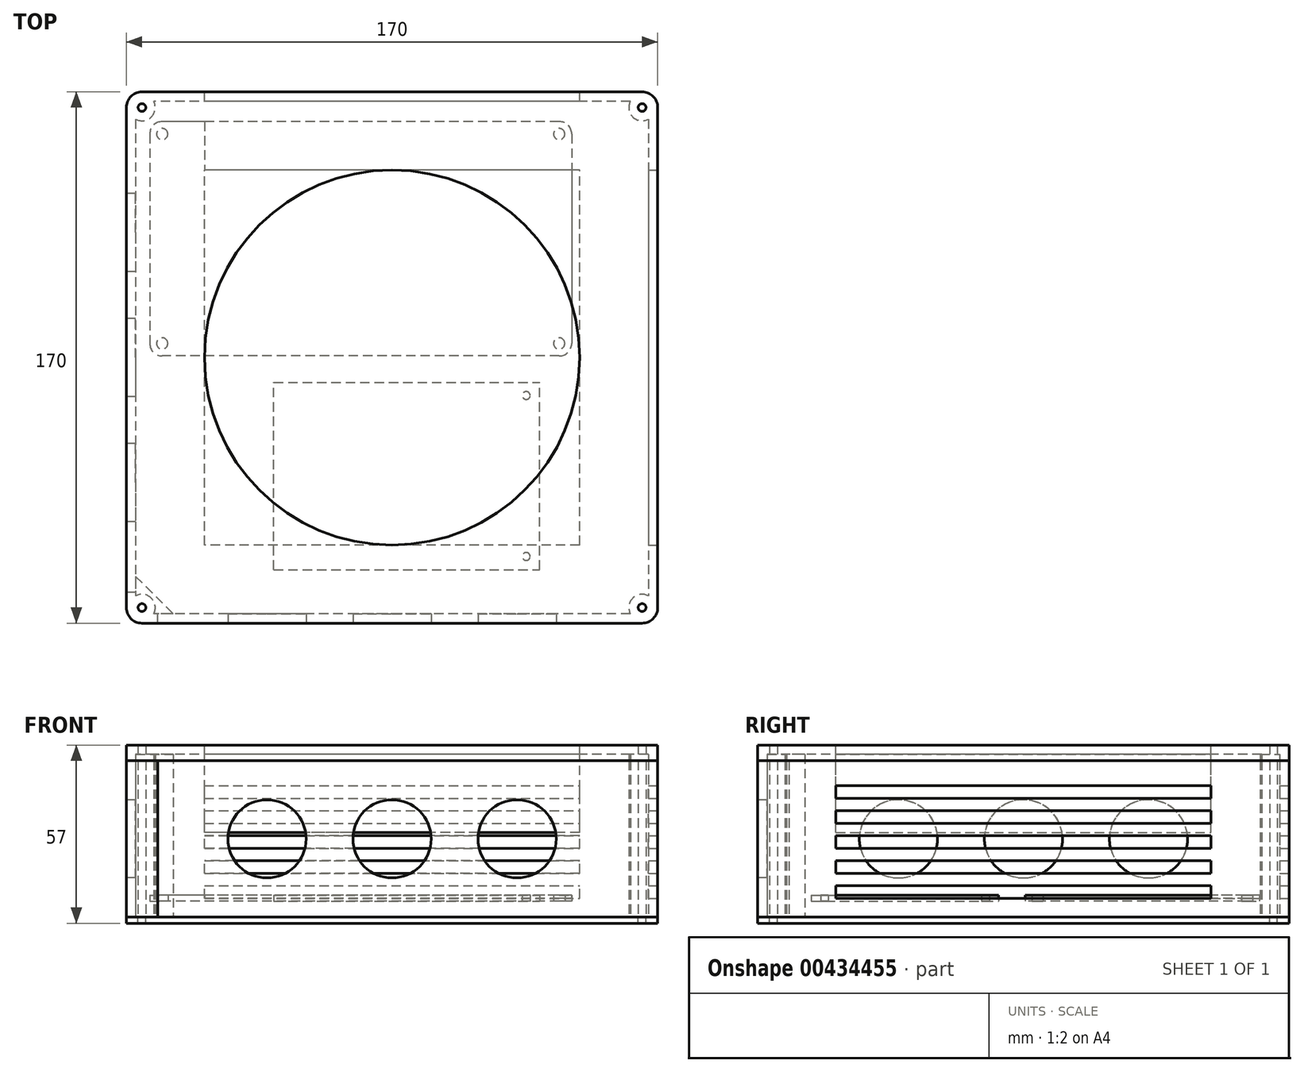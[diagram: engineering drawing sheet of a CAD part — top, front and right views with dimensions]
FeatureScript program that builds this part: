
annotation { "Feature Type Name" : "Feature", "Feature Type Description" : "" }
export const myFeature = defineFeature(function(context is Context, id is Id, definition is map)
    precondition{}
    {
        {
            var Q0;
            Q0=qCreatedBy(makeId("Top.planeOp"),FACE);
            var sketch = newSketch(context, id + "F0", { "sketchPlane" : qUnion([Q0])});
            skLineSegment(sketch, "E0.bottom", {"start": v(63.5, 37.5) * mm, "end": v(-63.5, 37.5) * mm});
            skLineSegment(sketch, "E0.top", {"start": v(63.5, -37.5) * mm, "end": v(-63.5, -37.5) * mm});
            skLineSegment(sketch, "E0.left", {"start": v(67.5, 33.5) * mm, "end": v(67.5, -33.5) * mm});
            skLineSegment(sketch, "E0.right", {"start": v(-67.5, 33.5) * mm, "end": v(-67.5, -33.5) * mm});
            skPoint(sketch, "E0.middle", {"position": v(0, 0) * mm});
            skCircle(sketch, "E1", {"center": v(63.5, 33.5) * mm, "radius": 1.8 * mm});
            skCircle(sketch, "E2.MirrorC", {"center": v(-63.5, 33.5) * mm, "radius": 1.8 * mm});
            skCircle(sketch, "E3.MirrorC", {"center": v(63.5, -33.5) * mm, "radius": 1.8 * mm});
            skCircle(sketch, "E4.MirrorC", {"center": v(-63.5, -33.5) * mm, "radius": 1.8 * mm});
            skPoint(sketch, "E5.visualSharp", {"position": v(-67.5, 37.5) * mm});
            skArc(sketch, "E5.filletArc", {"start": v(-63.5, 37.5) * mm, "mid": v(-66.33, 36.33) * mm, "end": v(-67.5, 33.5) * mm});
            skPoint(sketch, "E6.visualSharp", {"position": v(-67.5, -37.5) * mm});
            skArc(sketch, "E6.filletArc", {"start": v(-67.5, -33.5) * mm, "mid": v(-66.33, -36.33) * mm, "end": v(-63.5, -37.5) * mm});
            skPoint(sketch, "E7.visualSharp", {"position": v(67.5, -37.5) * mm});
            skArc(sketch, "E7.filletArc", {"start": v(63.5, -37.5) * mm, "mid": v(66.33, -36.33) * mm, "end": v(67.5, -33.5) * mm});
            skPoint(sketch, "E8.visualSharp", {"position": v(67.5, 37.5) * mm});
            skArc(sketch, "E8.filletArc", {"start": v(67.5, 33.5) * mm, "mid": v(66.33, 36.33) * mm, "end": v(63.5, 37.5) * mm});
            skSolve(sketch);
        }
        {
            var Q0;
            Q0 = qSketchRegion(id + "F0", true);
            extrude(context, id + "F1", {"entities" : qUnion([Q0]), "depth" : 2 * mm});
        }
        {
            var Q0;
            Q0=qCreatedBy(makeId("Top.planeOp"),FACE);
            var sketch = newSketch(context, id + "F2", { "sketchPlane" : qUnion([Q0])});
            skLineSegment(sketch, "E9.bottom", {"start": v(-42.5, -30) * mm, "end": v(42.5, -30) * mm});
            skLineSegment(sketch, "E9.top", {"start": v(-42.5, 30) * mm, "end": v(42.5, 30) * mm});
            skLineSegment(sketch, "E9.left", {"start": v(-42.5, -30) * mm, "end": v(-42.5, 30) * mm});
            skLineSegment(sketch, "E9.right", {"start": v(42.5, -30) * mm, "end": v(42.5, 30) * mm});
            skPoint(sketch, "E9.middle", {"position": v(0, 0) * mm});
            skCircle(sketch, "E10", {"center": v(38.25, -25.75) * mm, "radius": 1.25 * mm});
            skCircle(sketch, "E11.MirrorC", {"center": v(38.25, 25.75) * mm, "radius": 1.25 * mm});
            skSolve(sketch);
        }
        {
            var Q0;
            Q0=makeQuery(id+"F2.imprint","IMPRINT",FACE,{"disambiguationData":[TD([[makeQuery(id+"F2.imprint","IMPRINT",EDGE,{"derivedFrom":sQuery(id+"F2.wireOp",EDGE,"E9.bottom")}),1.0]])]});
            extrude(context, id + "F3", {"entities" : qUnion([Q0]), "depth" : 2 * mm});
        }
        {
            var Q0;
            Q0=makeQuery(id+"F1.opExtrude","SWEPT_BODY",BODY,{"disambiguationData":[OSD([sQuery(id+"F0.wireOp",EDGE,"E0.bottom"),sQuery(id+"F0.wireOp",EDGE,"E0.top"),sQuery(id+"F0.wireOp",EDGE,"E0.left"),sQuery(id+"F0.wireOp",EDGE,"E0.right"),sQuery(id+"F0.wireOp",EDGE,"E1"),sQuery(id+"F0.wireOp",EDGE,"E2.MirrorC"),sQuery(id+"F0.wireOp",EDGE,"E3.MirrorC"),sQuery(id+"F0.wireOp",EDGE,"E4.MirrorC"),sQuery(id+"F0.wireOp",EDGE,"E5.filletArc"),sQuery(id+"F0.wireOp",EDGE,"E6.filletArc"),sQuery(id+"F0.wireOp",EDGE,"E7.filletArc"),sQuery(id+"F0.wireOp",EDGE,"E8.filletArc")])]});
            transform(context, id + "F4", {"entities" : qUnion([Q0]), "transformType" : TransformType.TRANSLATION_3D, "dx" : -10 * mm, "dy" : 38 * mm, "dz" : 5 * mm, "makeCopy" : false});
        }
        {
            var Q0;
            Q0=makeQuery(id+"F3.opExtrude","SWEPT_BODY",BODY,{"disambiguationData":[OSD([sQuery(id+"F2.wireOp",EDGE,"E9.bottom"),sQuery(id+"F2.wireOp",EDGE,"E9.top"),sQuery(id+"F2.wireOp",EDGE,"E9.left"),sQuery(id+"F2.wireOp",EDGE,"E9.right"),sQuery(id+"F2.wireOp",EDGE,"E10"),sQuery(id+"F2.wireOp",EDGE,"E11.MirrorC")])]});
            transform(context, id + "F5", {"entities" : qUnion([Q0]), "transformType" : TransformType.TRANSLATION_3D, "dx" : 4.7 * mm, "dy" : -37.9 * mm, "dz" : 5 * mm, "makeCopy" : false});
        }
        {
            var Q0;
            Q0=qCreatedBy(makeId("Top.planeOp"),FACE);
            var sketch = newSketch(context, id + "F6", { "sketchPlane" : qUnion([Q0])});
            skLineSegment(sketch, "E12.bottom", {"start": v(85, 85) * mm, "end": v(-85, 85) * mm});
            skLineSegment(sketch, "E12.top", {"start": v(85, -85) * mm, "end": v(-85, -85) * mm});
            skLineSegment(sketch, "E12.left", {"start": v(85, 85) * mm, "end": v(85, -85) * mm});
            skLineSegment(sketch, "E12.right", {"start": v(-85, 85) * mm, "end": v(-85, -85) * mm});
            skPoint(sketch, "E12.middle", {"position": v(0, 0) * mm});
            skCircle(sketch, "E13", {"center": v(-80, -80) * mm, "radius": 1.25 * mm});
            skCircle(sketch, "E14.MirrorC", {"center": v(-80, 80) * mm, "radius": 1.25 * mm});
            skCircle(sketch, "E15.MirrorC", {"center": v(80, -80) * mm, "radius": 1.25 * mm});
            skCircle(sketch, "E16.MirrorC", {"center": v(80, 80) * mm, "radius": 1.25 * mm});
            skSolve(sketch);
        }
        {
            var Q0;
            Q0 = qSketchRegion(id + "F6", true);
            extrude(context, id + "F7", {"entities" : qUnion([Q0]), "depth" : 50 * mm, "offsetDistance" : 25 * mm});
        }
        {
            var Q0;
            Q0=makeQuery(id+"F7.opExtrude","CAP_FACE",FACE,{"disambiguationData":[OSD([sQuery(id+"F6.wireOp",EDGE,"E12.bottom"),sQuery(id+"F6.wireOp",EDGE,"E12.top"),sQuery(id+"F6.wireOp",EDGE,"E12.left"),sQuery(id+"F6.wireOp",EDGE,"E12.right"),sQuery(id+"F6.wireOp",EDGE,"E13"),sQuery(id+"F6.wireOp",EDGE,"E14.MirrorC"),sQuery(id+"F6.wireOp",EDGE,"E15.MirrorC"),sQuery(id+"F6.wireOp",EDGE,"E16.MirrorC")])],"isStart":false});
            var Q1;
            Q1=makeQuery(id+"F7.opExtrude","CAP_FACE",FACE,{"disambiguationData":[OSD([sQuery(id+"F6.wireOp",EDGE,"E12.bottom"),sQuery(id+"F6.wireOp",EDGE,"E12.top"),sQuery(id+"F6.wireOp",EDGE,"E12.left"),sQuery(id+"F6.wireOp",EDGE,"E12.right"),sQuery(id+"F6.wireOp",EDGE,"E13"),sQuery(id+"F6.wireOp",EDGE,"E14.MirrorC"),sQuery(id+"F6.wireOp",EDGE,"E15.MirrorC"),sQuery(id+"F6.wireOp",EDGE,"E16.MirrorC")])],"isStart":true});
            shell(context, id + "F8", {"entities" : qUnion([Q0, Q1]), "thickness" : 3 * mm});
        }
        {
            var Q0;
            Q0=makeQuery(id+"F7.opExtrude","SWEPT_FACE",FACE,{"disambiguationData":[OSD([sQuery(id+"F6.wireOp",EDGE,"E12.right")])]});
            var sketch = newSketch(context, id + "F9", { "sketchPlane" : qUnion([Q0])});
            skLineSegment(sketch, "E17.bottom", {"start": v(-15, 8) * mm, "end": v(-85, 8) * mm});
            skLineSegment(sketch, "E17.top", {"start": v(-15, 23) * mm, "end": v(-85, 23) * mm});
            skLineSegment(sketch, "E17.left", {"start": v(-15, 8) * mm, "end": v(-15, 23) * mm});
            skLineSegment(sketch, "E17.right", {"start": v(-85, 8) * mm, "end": v(-85, 23) * mm});
            skSolve(sketch);
        }
        {
            var Q0;
            Q0 = qSketchRegion(id + "F6", true);
            var Q1;
            Q1=makeQuery(id+"FItIViklihHbl3o_3.splitOp","SPLIT",FACE,{"derivedFrom":makeQuery(id+"FYmSAssxMf2Dcwc_3.splitOp","SPLIT",FACE,{"derivedFrom":makeQuery(id+"F7.opExtrude","CAP_FACE",FACE,{"disambiguationData":[OSD([sQuery(id+"F6.wireOp",EDGE,"E12.bottom"),sQuery(id+"F6.wireOp",EDGE,"E12.top"),sQuery(id+"F6.wireOp",EDGE,"E12.left"),sQuery(id+"F6.wireOp",EDGE,"E12.right"),sQuery(id+"F6.wireOp",EDGE,"E13"),sQuery(id+"F6.wireOp",EDGE,"E14.MirrorC"),sQuery(id+"F6.wireOp",EDGE,"E15.MirrorC"),sQuery(id+"F6.wireOp",EDGE,"E16.MirrorC")])],"isStart":false}),"isFromBackBody":true})});
            extrude(context, id + "F10", {"entities" : qUnion([Q0]), "depth" : 55 * mm, "hasSecondDirection" : true, "secondDirectionBound" : SecondDirectionBoundingType.UP_TO_SURFACE, "secondDirectionOppositeDirection" : false, "secondDirectionBoundEntityFace" : qUnion([Q1]), "secondDirectionDepth" : 55 * mm, "offsetDistance" : 25 * mm});
        }
        {
            var Q0;
            Q0 = qSketchRegion(id + "F6", true);
            extrude(context, id + "F11", {"entities" : qUnion([Q0]), "oppositeDirection" : true, "depth" : 2 * mm, "offsetDistance" : 25 * mm});
        }
        {
            var Q0;
            Q0=makeQuery(id+"F7.opExtrude","SWEPT_EDGE",EDGE,{"disambiguationData":[OSD([sQuery(id+"F6.wireOp",EDGE,"E12.top"),sQuery(id+"F6.wireOp",EDGE,"E12.right")])]});
            var Q1;
            Q1=makeQuery(id+"F7.opExtrude","SWEPT_EDGE",EDGE,{"disambiguationData":[OSD([sQuery(id+"F6.wireOp",EDGE,"E12.top"),sQuery(id+"F6.wireOp",EDGE,"E12.left")])]});
            var Q2;
            Q2=makeQuery(id+"F7.opExtrude","SWEPT_EDGE",EDGE,{"disambiguationData":[OSD([sQuery(id+"F6.wireOp",EDGE,"E12.bottom"),sQuery(id+"F6.wireOp",EDGE,"E12.left")])]});
            var Q3;
            Q3=makeQuery(id+"F7.opExtrude","SWEPT_EDGE",EDGE,{"disambiguationData":[OSD([sQuery(id+"F6.wireOp",EDGE,"E12.bottom"),sQuery(id+"F6.wireOp",EDGE,"E12.right")])]});
            var Q4;
            Q4=makeQuery(id+"F11.opExtrude","SWEPT_EDGE",EDGE,{"disambiguationData":[OSD([sQuery(id+"F6.wireOp",EDGE,"E12.bottom"),sQuery(id+"F6.wireOp",EDGE,"E12.left")])]});
            var Q5;
            Q5=makeQuery(id+"F10.opExtrude","SWEPT_EDGE",EDGE,{"disambiguationData":[OSD([sQuery(id+"F6.wireOp",EDGE,"E12.bottom"),sQuery(id+"F6.wireOp",EDGE,"E12.left")])]});
            var Q6;
            Q6=makeQuery(id+"F11.opExtrude","SWEPT_EDGE",EDGE,{"disambiguationData":[OSD([sQuery(id+"F6.wireOp",EDGE,"E12.bottom"),sQuery(id+"F6.wireOp",EDGE,"E12.right")])]});
            var Q7;
            Q7=makeQuery(id+"F10.opExtrude","SWEPT_EDGE",EDGE,{"disambiguationData":[OSD([sQuery(id+"F6.wireOp",EDGE,"E12.bottom"),sQuery(id+"F6.wireOp",EDGE,"E12.right")])]});
            var Q8;
            Q8=makeQuery(id+"F10.opExtrude","SWEPT_EDGE",EDGE,{"disambiguationData":[OSD([sQuery(id+"F6.wireOp",EDGE,"E12.top"),sQuery(id+"F6.wireOp",EDGE,"E12.right")])]});
            var Q9;
            Q9=makeQuery(id+"F11.opExtrude","SWEPT_EDGE",EDGE,{"disambiguationData":[OSD([sQuery(id+"F6.wireOp",EDGE,"E12.top"),sQuery(id+"F6.wireOp",EDGE,"E12.right")])]});
            var Q10;
            Q10=makeQuery(id+"F10.opExtrude","SWEPT_EDGE",EDGE,{"disambiguationData":[OSD([sQuery(id+"F6.wireOp",EDGE,"E12.top"),sQuery(id+"F6.wireOp",EDGE,"E12.left")])]});
            var Q11;
            Q11=makeQuery(id+"F11.opExtrude","SWEPT_EDGE",EDGE,{"disambiguationData":[OSD([sQuery(id+"F6.wireOp",EDGE,"E12.top"),sQuery(id+"F6.wireOp",EDGE,"E12.left")])]});
            fillet(context, id + "F12", {"entities" : qUnion([Q0, Q1, Q2, Q3, Q4, Q5, Q6, Q7, Q8, Q9, Q10, Q11]), "radius" : 5 * mm, "tangentPropagation" : true, "allowEdgeOverflow" : false});
        }
        {
            var Q0;
            Q0=makeQuery(id+"F10.opExtrude","CAP_FACE",FACE,{"disambiguationData":[OSD([sQuery(id+"F6.wireOp",EDGE,"E12.bottom"),sQuery(id+"F6.wireOp",EDGE,"E12.top"),sQuery(id+"F6.wireOp",EDGE,"E12.left"),sQuery(id+"F6.wireOp",EDGE,"E12.right"),sQuery(id+"F6.wireOp",EDGE,"E13"),sQuery(id+"F6.wireOp",EDGE,"E14.MirrorC"),sQuery(id+"F6.wireOp",EDGE,"E15.MirrorC"),sQuery(id+"F6.wireOp",EDGE,"E16.MirrorC")])],"isStart":true});
            shell(context, id + "F13", {"entities" : qUnion([Q0]), "thickness" : 3 * mm});
        }
        {
            var Q0;
            Q0=makeQuery(id+"F10.opExtrude","CAP_FACE",FACE,{"disambiguationData":[OSD([sQuery(id+"F6.wireOp",EDGE,"E12.bottom"),sQuery(id+"F6.wireOp",EDGE,"E12.top"),sQuery(id+"F6.wireOp",EDGE,"E12.left"),sQuery(id+"F6.wireOp",EDGE,"E12.right"),sQuery(id+"F6.wireOp",EDGE,"E13"),sQuery(id+"F6.wireOp",EDGE,"E14.MirrorC"),sQuery(id+"F6.wireOp",EDGE,"E15.MirrorC"),sQuery(id+"F6.wireOp",EDGE,"E16.MirrorC")])],"isStart":false});
            var sketch = newSketch(context, id + "F14", { "sketchPlane" : qUnion([Q0])});
            skCircle(sketch, "E18", {"center": v(0, 0) * mm, "radius": 60 * mm});
            skSolve(sketch);
        }
        {
            var Q0;
            Q0 = qSketchRegion(id + "F14", true);
            extrude(context, id + "F15", {"entities" : qUnion([Q0]), "operationType" : NewBodyOperationType.REMOVE, "oppositeDirection" : true, "depth" : 25 * mm});
        }
        {
            var Q0;
            Q0=makeQuery(id+"F13.opShell","OFFSET_FACE",FACE,{"disambiguationData":[OSD([sQuery(id+"F6.wireOp",EDGE,"E12.bottom"),sQuery(id+"F6.wireOp",EDGE,"E12.top"),sQuery(id+"F6.wireOp",EDGE,"E12.left"),sQuery(id+"F6.wireOp",EDGE,"E12.right"),sQuery(id+"F6.wireOp",EDGE,"E13"),sQuery(id+"F6.wireOp",EDGE,"E14.MirrorC"),sQuery(id+"F6.wireOp",EDGE,"E15.MirrorC"),sQuery(id+"F6.wireOp",EDGE,"E16.MirrorC")])]});
            var sketch = newSketch(context, id + "F16", { "sketchPlane" : qUnion([Q0])});
            skLineSegment(sketch, "E19.bottom", {"start": v(60, 60) * mm, "end": v(-60, 60) * mm});
            skLineSegment(sketch, "E19.top", {"start": v(60, -60) * mm, "end": v(-60, -60) * mm});
            skLineSegment(sketch, "E19.left", {"start": v(60, 60) * mm, "end": v(60, -60) * mm});
            skLineSegment(sketch, "E19.right", {"start": v(-60, 60) * mm, "end": v(-60, -60) * mm});
            skPoint(sketch, "E19.middle", {"position": v(0, 0) * mm});
            skSolve(sketch);
        }
        {
            var Q0;
            Q0 = qSketchRegion(id + "F16", true);
            extrude(context, id + "F17", {"entities" : qUnion([Q0]), "depth" : 25 * mm});
        }
        {
            var Q0;
            Q0=makeQuery(id+"F7.opExtrude","SWEPT_FACE",FACE,{"disambiguationData":[OSD([sQuery(id+"F6.wireOp",EDGE,"E12.left")])]});
            var sketch = newSketch(context, id + "F18", { "sketchPlane" : qUnion([Q0])});
            skLineSegment(sketch, "E20.bottom", {"start": v(60, 6) * mm, "end": v(-60, 6) * mm});
            skLineSegment(sketch, "E20.top", {"start": v(60, 10) * mm, "end": v(-60, 10) * mm});
            skLineSegment(sketch, "E20.left", {"start": v(60, 6) * mm, "end": v(60, 10) * mm});
            skLineSegment(sketch, "E20.right", {"start": v(-60, 6) * mm, "end": v(-60, 10) * mm});
            skPoint(sketch, "E20.middle", {"position": v(0, 8) * mm});
            skLineSegment(sketch, "E21.0.1.0", {"start": v(60, 18) * mm, "end": v(-60, 18) * mm});
            skLineSegment(sketch, "E21.0.1.1", {"start": v(-60, 14) * mm, "end": v(-60, 18) * mm});
            skLineSegment(sketch, "E21.0.1.2", {"start": v(60, 14) * mm, "end": v(-60, 14) * mm});
            skLineSegment(sketch, "E21.0.1.3", {"start": v(60, 14) * mm, "end": v(60, 18) * mm});
            skLineSegment(sketch, "E21.0.2.0", {"start": v(60, 26) * mm, "end": v(-60, 26) * mm});
            skLineSegment(sketch, "E21.0.2.1", {"start": v(-60, 22) * mm, "end": v(-60, 26) * mm});
            skLineSegment(sketch, "E21.0.2.2", {"start": v(60, 22) * mm, "end": v(-60, 22) * mm});
            skLineSegment(sketch, "E21.0.2.3", {"start": v(60, 22) * mm, "end": v(60, 26) * mm});
            skLineSegment(sketch, "E21.0.3.0", {"start": v(60, 34) * mm, "end": v(-60, 34) * mm});
            skLineSegment(sketch, "E21.0.3.1", {"start": v(-60, 30) * mm, "end": v(-60, 34) * mm});
            skLineSegment(sketch, "E21.0.3.2", {"start": v(60, 30) * mm, "end": v(-60, 30) * mm});
            skLineSegment(sketch, "E21.0.3.3", {"start": v(60, 30) * mm, "end": v(60, 34) * mm});
            skLineSegment(sketch, "E21.0.4.0", {"start": v(60, 42) * mm, "end": v(-60, 42) * mm});
            skLineSegment(sketch, "E21.0.4.1", {"start": v(-60, 38) * mm, "end": v(-60, 42) * mm});
            skLineSegment(sketch, "E21.0.4.2", {"start": v(60, 38) * mm, "end": v(-60, 38) * mm});
            skLineSegment(sketch, "E21.0.4.3", {"start": v(60, 38) * mm, "end": v(60, 42) * mm});
            skLineSegment(sketch, "E21.direction1", {"start": v(-60, 10) * mm, "end": v(-35, 10) * mm, "construction": true});
            skLineSegment(sketch, "E21.direction2", {"start": v(-60, 10) * mm, "end": v(-60, 18) * mm, "construction": true});
            skSolve(sketch);
        }
        {
            var Q0;
            Q0=makeQuery(id+"F7.opExtrude","SWEPT_FACE",FACE,{"disambiguationData":[OSD([sQuery(id+"F6.wireOp",EDGE,"E12.bottom")])]});
            var sketch = newSketch(context, id + "F19", { "sketchPlane" : qUnion([Q0])});
            skLineSegment(sketch, "E22.bottom", {"start": v(60, 6) * mm, "end": v(-60, 6) * mm});
            skLineSegment(sketch, "E22.top", {"start": v(60, 10) * mm, "end": v(-60, 10) * mm});
            skLineSegment(sketch, "E22.left", {"start": v(60, 6) * mm, "end": v(60, 10) * mm});
            skLineSegment(sketch, "E22.right", {"start": v(-60, 6) * mm, "end": v(-60, 10) * mm});
            skPoint(sketch, "E22.middle", {"position": v(0, 8) * mm});
            skLineSegment(sketch, "E23.0.1.0", {"start": v(60, 18) * mm, "end": v(-60, 18) * mm});
            skLineSegment(sketch, "E23.0.1.1", {"start": v(-60, 14) * mm, "end": v(-60, 18) * mm});
            skLineSegment(sketch, "E23.0.1.2", {"start": v(60, 14) * mm, "end": v(-60, 14) * mm});
            skLineSegment(sketch, "E23.0.1.3", {"start": v(60, 14) * mm, "end": v(60, 18) * mm});
            skLineSegment(sketch, "E23.0.2.0", {"start": v(60, 26) * mm, "end": v(-60, 26) * mm});
            skLineSegment(sketch, "E23.0.2.1", {"start": v(-60, 22) * mm, "end": v(-60, 26) * mm});
            skLineSegment(sketch, "E23.0.2.2", {"start": v(60, 22) * mm, "end": v(-60, 22) * mm});
            skLineSegment(sketch, "E23.0.2.3", {"start": v(60, 22) * mm, "end": v(60, 26) * mm});
            skLineSegment(sketch, "E23.0.3.0", {"start": v(60, 34) * mm, "end": v(-60, 34) * mm});
            skLineSegment(sketch, "E23.0.3.1", {"start": v(-60, 30) * mm, "end": v(-60, 34) * mm});
            skLineSegment(sketch, "E23.0.3.2", {"start": v(60, 30) * mm, "end": v(-60, 30) * mm});
            skLineSegment(sketch, "E23.0.3.3", {"start": v(60, 30) * mm, "end": v(60, 34) * mm});
            skLineSegment(sketch, "E23.0.4.0", {"start": v(60, 42) * mm, "end": v(-60, 42) * mm});
            skLineSegment(sketch, "E23.0.4.1", {"start": v(-60, 38) * mm, "end": v(-60, 42) * mm});
            skLineSegment(sketch, "E23.0.4.2", {"start": v(60, 38) * mm, "end": v(-60, 38) * mm});
            skLineSegment(sketch, "E23.0.4.3", {"start": v(60, 38) * mm, "end": v(60, 42) * mm});
            skLineSegment(sketch, "E23.direction1", {"start": v(-60, 10) * mm, "end": v(-30.33, 10) * mm, "construction": true});
            skLineSegment(sketch, "E23.direction2", {"start": v(-60, 10) * mm, "end": v(-60, 18) * mm, "construction": true});
            skSolve(sketch);
        }
        {
            var Q0;
            Q0 = qSketchRegion(id + "F18", true);
            extrude(context, id + "F20", {"entities" : qUnion([Q0]), "operationType" : NewBodyOperationType.REMOVE, "oppositeDirection" : true, "depth" : 25 * mm, "offsetDistance" : 25 * mm});
        }
        {
            var Q0;
            Q0 = qSketchRegion(id + "F19", true);
            extrude(context, id + "F21", {"entities" : qUnion([Q0]), "operationType" : NewBodyOperationType.REMOVE, "oppositeDirection" : true, "depth" : 25 * mm, "offsetDistance" : 25 * mm});
        }
        {
            var Q0;
            Q0=makeQuery(id+"F7.opExtrude","SWEPT_FACE",FACE,{"disambiguationData":[OSD([sQuery(id+"F6.wireOp",EDGE,"E12.right")])]});
            var sketch = newSketch(context, id + "F22", { "sketchPlane" : qUnion([Q0])});
            skCircle(sketch, "E24", {"center": v(0, 25) * mm, "radius": 12.5 * mm});
            skCircle(sketch, "E25", {"center": v(40, 25) * mm, "radius": 12.5 * mm});
            skCircle(sketch, "E26", {"center": v(-40, 25) * mm, "radius": 12.5 * mm});
            skSolve(sketch);
        }
        {
            var Q0;
            Q0=makeQuery(id+"F7.opExtrude","SWEPT_FACE",FACE,{"disambiguationData":[OSD([sQuery(id+"F6.wireOp",EDGE,"E12.top")])]});
            var sketch = newSketch(context, id + "F23", { "sketchPlane" : qUnion([Q0])});
            skCircle(sketch, "E27", {"center": v(0, 25) * mm, "radius": 12.5 * mm});
            skCircle(sketch, "E28", {"center": v(40, 25) * mm, "radius": 12.5 * mm});
            skCircle(sketch, "E29", {"center": v(-40, 25) * mm, "radius": 12.5 * mm});
            skSolve(sketch);
        }
        {
            var Q0;
            Q0 = qSketchRegion(id + "F23", true);
            extrude(context, id + "F24", {"entities" : qUnion([Q0]), "operationType" : NewBodyOperationType.REMOVE, "oppositeDirection" : true, "depth" : 25 * mm, "offsetDistance" : 25 * mm});
        }
        {
            var Q0;
            Q0 = qSketchRegion(id + "F22", true);
            extrude(context, id + "F25", {"entities" : qUnion([Q0]), "operationType" : NewBodyOperationType.REMOVE, "oppositeDirection" : true, "depth" : 25 * mm, "offsetDistance" : 25 * mm});
        }
        {
            var Q0;
            Q0=makeQuery(id+"F11.opExtrude","CAP_FACE",FACE,{"disambiguationData":[OSD([sQuery(id+"F6.wireOp",EDGE,"E12.bottom"),sQuery(id+"F6.wireOp",EDGE,"E12.top"),sQuery(id+"F6.wireOp",EDGE,"E12.left"),sQuery(id+"F6.wireOp",EDGE,"E12.right"),sQuery(id+"F6.wireOp",EDGE,"E13"),sQuery(id+"F6.wireOp",EDGE,"E14.MirrorC"),sQuery(id+"F6.wireOp",EDGE,"E15.MirrorC"),sQuery(id+"F6.wireOp",EDGE,"E16.MirrorC")])],"isStart":true});
            var sketch = newSketch(context, id + "F26", { "sketchPlane" : qUnion([Q0])});
            skCircle(sketch, "E30.0", {"center": v(-80, -80) * mm, "radius": 1.25 * mm});
            skLineSegment(sketch, "E31", {"start": v(-80, -85) * mm, "end": v(-75, -85) * mm});
            skLineSegment(sketch, "E32", {"start": v(-75, -85) * mm, "end": v(-75, -82) * mm});
            skLineSegment(sketch, "E33", {"start": v(-75, -82) * mm, "end": v(-70, -82) * mm});
            skLineSegment(sketch, "E34", {"start": v(-83.54, -83.54) * mm, "end": v(-80, -80) * mm, "construction": true});
            skLineSegment(sketch, "E35.MirrorCS", {"start": v(-85, -80) * mm, "end": v(-85, -75) * mm});
            skLineSegment(sketch, "E36.MirrorCS", {"start": v(-85, -75) * mm, "end": v(-82, -75) * mm});
            skLineSegment(sketch, "E37.MirrorCS", {"start": v(-82, -75) * mm, "end": v(-82, -70) * mm});
            skLineSegment(sketch, "E38", {"start": v(-82, -70) * mm, "end": v(-70, -82) * mm});
            skSolve(sketch);
        }
        {
            var Q0;
            Q0=makeQuery(id+"F26.imprint","IMPRINT",FACE,{"disambiguationData":[TD([[makeQuery(id+"F26.imprint","IMPRINT",EDGE,{"derivedFrom":sQuery(id+"F26.wireOp",EDGE,"E30.0")}),-1.0]])]});
            extrude(context, id + "F27", {"entities" : qUnion([Q0]), "endBound" : BoundingType.UP_TO_NEXT, "depth" : 25 * mm, "offsetDistance" : 25 * mm});
        }
    });
